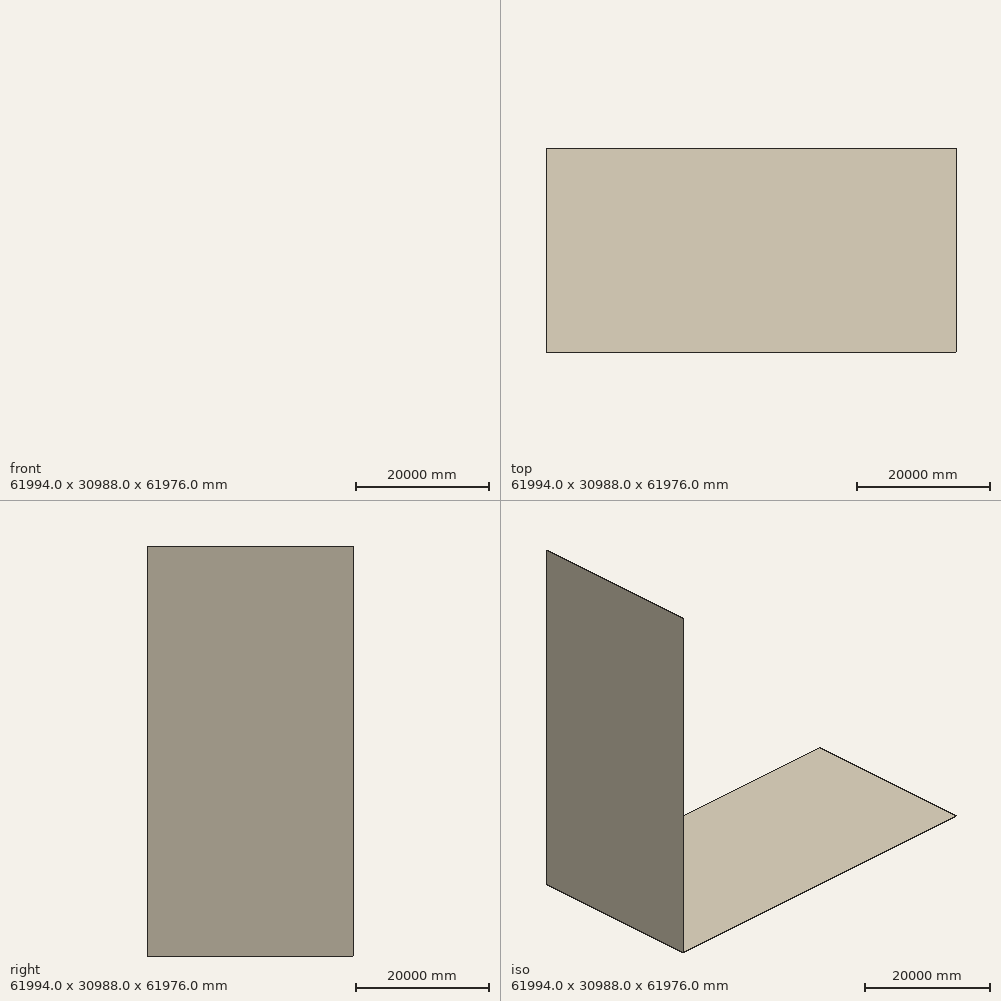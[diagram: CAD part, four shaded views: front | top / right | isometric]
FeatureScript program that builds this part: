
annotation { "Feature Type Name" : "Feature", "Feature Type Description" : "" }
export const myFeature = defineFeature(function(context is Context, id is Id, definition is map)
    precondition{}
    {
        {
            var Q0;
            Q0=qCreatedBy(makeId("Top.planeOp"),FACE);
            var sketch = newSketch(context, id + "F0", { "sketchPlane" : qUnion([Q0])});
            skLineSegment(sketch, "E0.bottom", {"start": v(0, 0) * mm, "end": v(61976, 0) * mm});
            skLineSegment(sketch, "E0.top", {"start": v(0, 30988) * mm, "end": v(61976, 30988) * mm});
            skLineSegment(sketch, "E0.left", {"start": v(0, 0) * mm, "end": v(0, 30988) * mm});
            skLineSegment(sketch, "E0.right", {"start": v(61976, 0) * mm, "end": v(61976, 30988) * mm});
            skSolve(sketch);
        }
        {
            var Q0;
            Q0=makeQuery(id+"F0.imprint","IMPRINT",FACE,{"disambiguationData":[TD([[makeQuery(id+"F0.imprint","IMPRINT",EDGE,{"derivedFrom":sQuery(id+"F0.wireOp",EDGE,"E0.bottom")}),1.0]])]});
            extrude(context, id + "F1", {"entities" : qUnion([Q0]), "depth" : 25 * mm, "offsetDistance" : 25.4 * mm});
        }
        {
            var Q0;
            Q0=qCreatedBy(makeId("Right.planeOp"),FACE);
            var sketch = newSketch(context, id + "F2", { "sketchPlane" : qUnion([Q0])});
            skLineSegment(sketch, "E1.bottom", {"start": v(0, 0) * mm, "end": v(30988, 0) * mm});
            skLineSegment(sketch, "E1.top", {"start": v(0, 61976) * mm, "end": v(30988, 61976) * mm});
            skLineSegment(sketch, "E1.left", {"start": v(0, 0) * mm, "end": v(0, 61976) * mm});
            skLineSegment(sketch, "E1.right", {"start": v(30988, 0) * mm, "end": v(30988, 61976) * mm});
            skSolve(sketch);
        }
        {
            var Q0;
            Q0=makeQuery(id+"F2.imprint","IMPRINT",FACE,{"disambiguationData":[TD([[makeQuery(id+"F2.imprint","IMPRINT",EDGE,{"derivedFrom":sQuery(id+"F2.wireOp",EDGE,"E1.bottom")}),1.0]])]});
            extrude(context, id + "F3", {"entities" : qUnion([Q0]), "operationType" : NewBodyOperationType.ADD, "oppositeDirection" : true, "depth" : 18 * mm, "offsetDistance" : 25.4 * mm});
        }
    });
